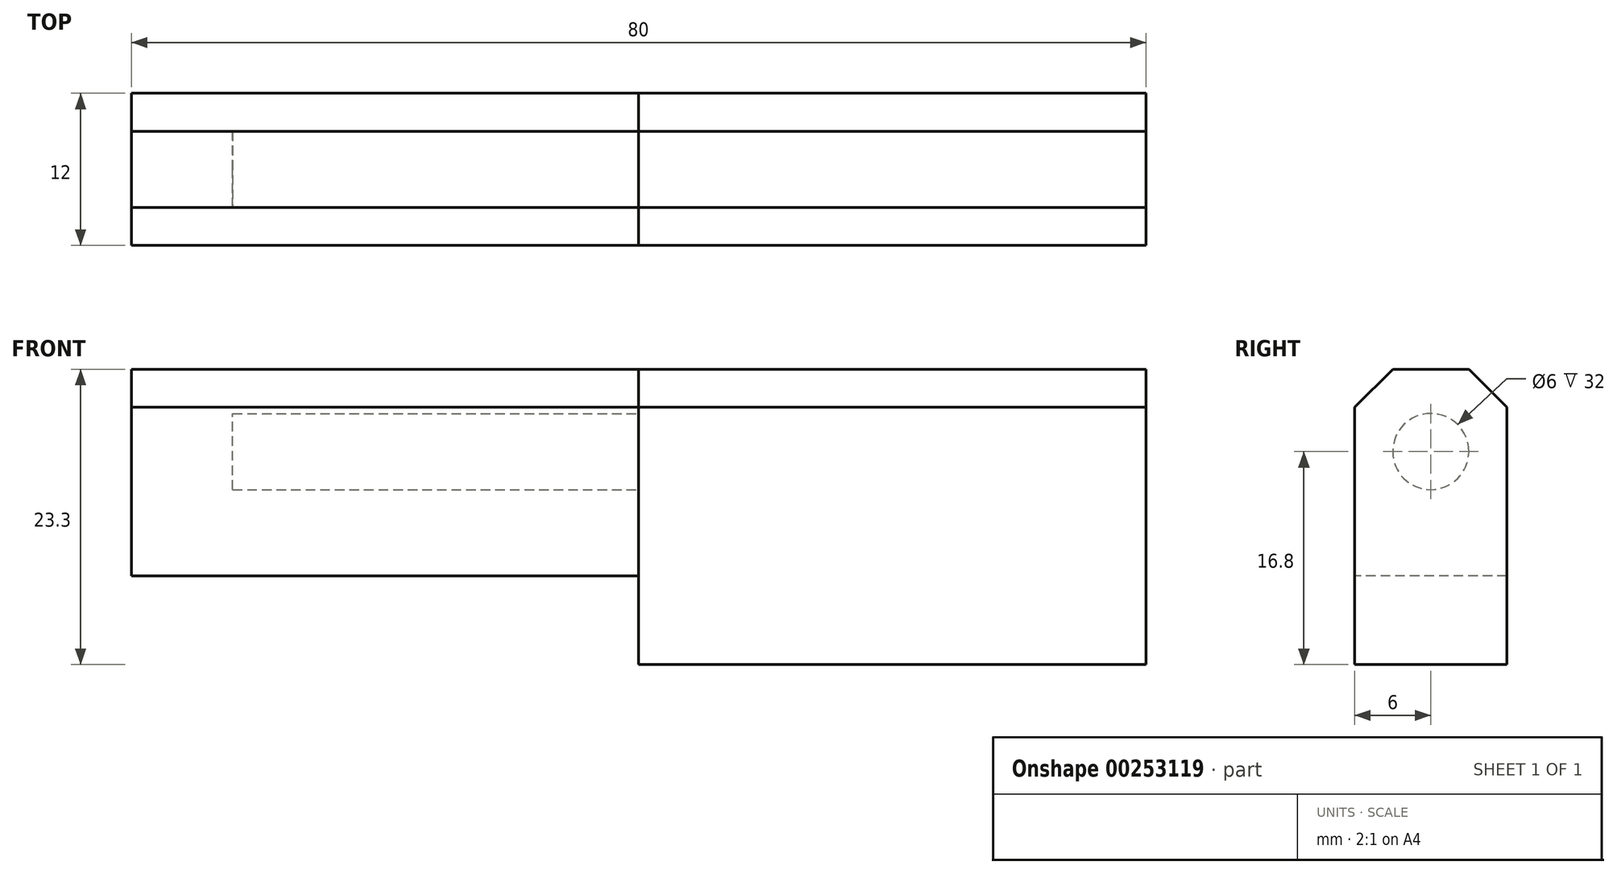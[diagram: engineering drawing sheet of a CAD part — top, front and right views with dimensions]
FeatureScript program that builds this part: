
annotation { "Feature Type Name" : "Feature", "Feature Type Description" : "" }
export const myFeature = defineFeature(function(context is Context, id is Id, definition is map)
    precondition{}
    {
        {
            var Q0;
            Q0=qCreatedBy(makeId("Right.planeOp"),FACE);
            var sketch = newSketch(context, id + "F0", { "sketchPlane" : qUnion([Q0])});
            skLineSegment(sketch, "E0", {"start": v(-6, 0) * mm, "end": v(-6, 20.3) * mm});
            skLineSegment(sketch, "E1", {"start": v(-6, 20.3) * mm, "end": v(-3, 23.3) * mm});
            skLineSegment(sketch, "E2", {"start": v(-3, 23.3) * mm, "end": v(3, 23.3) * mm});
            skLineSegment(sketch, "E3", {"start": v(3, 23.3) * mm, "end": v(6, 20.3) * mm});
            skLineSegment(sketch, "E4", {"start": v(6, 20.3) * mm, "end": v(6, 0) * mm});
            skLineSegment(sketch, "E5", {"start": v(6, 0) * mm, "end": v(-6, 0) * mm});
            skLineSegment(sketch, "E6", {"start": v(0, 23.3) * mm, "end": v(0, 0) * mm, "construction": true});
            skPoint(sketch, "E7", {"position": v(0, 16.8) * mm});
            skSolve(sketch);
        }
        {
            var Q0;
            Q0 = qSketchRegion(id + "F0", true);
            extrude(context, id + "F1", {"entities" : qUnion([Q0]), "depth" : 40 * mm});
        }
        {
            var Q0;
            Q0=makeQuery(id+"F0.imprint","IMPRINT",FACE,{"disambiguationData":[TD([[makeQuery(id+"F0.imprint","IMPRINT",EDGE,{"derivedFrom":sQuery(id+"F0.wireOp",EDGE,"E0")}),-1.0]])]});
            var sketch = newSketch(context, id + "F2", { "sketchPlane" : qUnion([Q0])});
            skCircle(sketch, "E8", {"center": v(0, 16.8) * mm, "radius": 2.98 * mm});
            skSolve(sketch);
        }
        {
            var Q0;
            Q0 = qSketchRegion(id + "F2", true);
            extrude(context, id + "F3", {"entities" : qUnion([Q0]), "operationType" : NewBodyOperationType.ADD, "oppositeDirection" : true, "depth" : 32 * mm});
        }
        {
            var Q0;
            Q0=makeQuery(id+"F3.opExtrude","CAP_EDGE",EDGE,{"disambiguationData":[OSD([sQuery(id+"F2.wireOp",EDGE,"E8")])],"isStart":false});
            chamfer(context, id + "F4", {"entities" : qUnion([Q0]), "width" : 1 * mm, "tangentPropagation" : true});
        }
        {
            var Q0;
            Q0=makeQuery(id+"F0.imprint","IMPRINT",FACE,{"disambiguationData":[TD([[makeQuery(id+"F0.imprint","IMPRINT",EDGE,{"derivedFrom":sQuery(id+"F0.wireOp",EDGE,"E0")}),-1.0]])]});
            var sketch = newSketch(context, id + "F5", { "sketchPlane" : qUnion([Q0])});
            skLineSegment(sketch, "E9", {"start": v(-6, 7) * mm, "end": v(-6, 20.3) * mm});
            skLineSegment(sketch, "E10", {"start": v(-6, 20.3) * mm, "end": v(-3, 23.3) * mm});
            skLineSegment(sketch, "E11", {"start": v(-3, 23.3) * mm, "end": v(3, 23.3) * mm});
            skLineSegment(sketch, "E12", {"start": v(3, 23.3) * mm, "end": v(6, 20.3) * mm});
            skLineSegment(sketch, "E13", {"start": v(6, 20.3) * mm, "end": v(6, 7) * mm});
            skLineSegment(sketch, "E14", {"start": v(6, 7) * mm, "end": v(-6, 7) * mm});
            skLineSegment(sketch, "E15", {"start": v(0, 23.3) * mm, "end": v(0, 7) * mm, "construction": true});
            skPoint(sketch, "E16", {"position": v(0, 16.8) * mm});
            skSolve(sketch);
        }
        {
            var Q0;
            Q0 = qSketchRegion(id + "F5", true);
            extrude(context, id + "F6", {"entities" : qUnion([Q0]), "oppositeDirection" : true, "depth" : 40 * mm});
        }
        {
            var Q0;
            Q0=makeQuery(id+"F0.imprint","IMPRINT",FACE,{"disambiguationData":[TD([[makeQuery(id+"F0.imprint","IMPRINT",EDGE,{"derivedFrom":sQuery(id+"F0.wireOp",EDGE,"E0")}),-1.0]])]});
            var sketch = newSketch(context, id + "F7", { "sketchPlane" : qUnion([Q0])});
            skCircle(sketch, "E17", {"center": v(0, 16.8) * mm, "radius": 3 * mm});
            skSolve(sketch);
        }
        {
            var Q0;
            Q0 = qSketchRegion(id + "F7", true);
            extrude(context, id + "F8", {"entities" : qUnion([Q0]), "operationType" : NewBodyOperationType.REMOVE, "oppositeDirection" : true, "depth" : 32 * mm});
        }
    });
